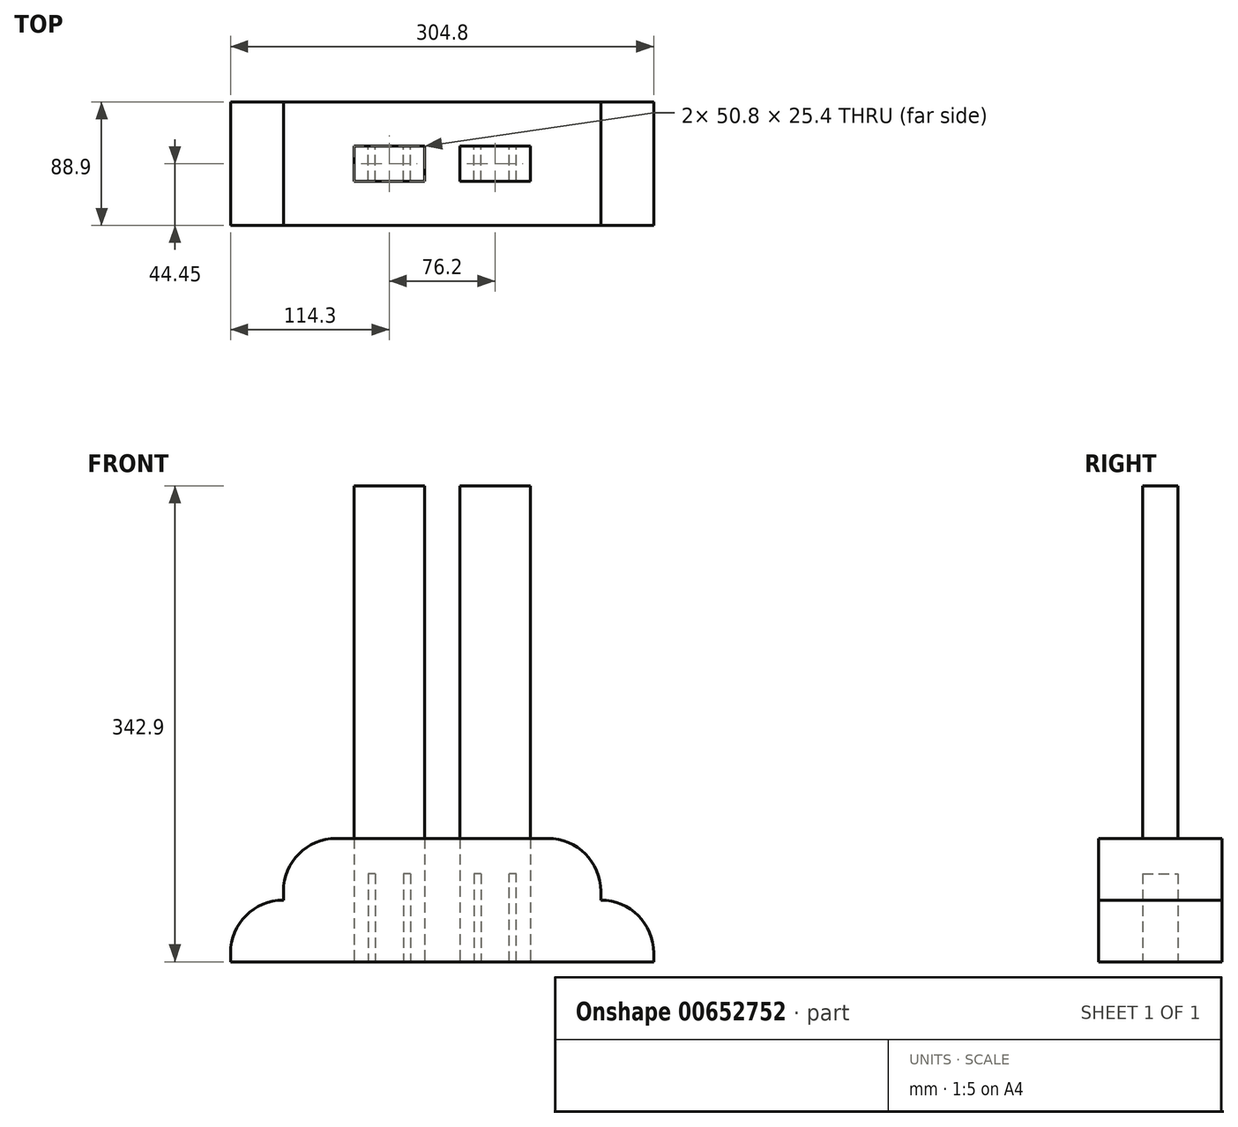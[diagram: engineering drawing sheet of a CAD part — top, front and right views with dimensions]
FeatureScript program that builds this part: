
annotation { "Feature Type Name" : "Feature", "Feature Type Description" : "" }
export const myFeature = defineFeature(function(context is Context, id is Id, definition is map)
    precondition{}
    {
        {
            var Q0;
            Q0=qCreatedBy(makeId("Front.planeOp"),FACE);
            var sketch = newSketch(context, id + "F0", { "sketchPlane" : qUnion([Q0])});
            skLineSegment(sketch, "E0.bottom", {"start": v(152.4, -44.45) * mm, "end": v(-152.4, -44.45) * mm});
            skLineSegment(sketch, "E0.top", {"start": v(76.2, 44.45) * mm, "end": v(-76.2, 44.45) * mm});
            skLineSegment(sketch, "E0.left", {"start": v(152.4, -44.45) * mm, "end": v(152.4, -38.1) * mm});
            skLineSegment(sketch, "E0.right", {"start": v(-152.4, -44.45) * mm, "end": v(-152.4, -38.1) * mm});
            skPoint(sketch, "E0.middle", {"position": v(0, 0) * mm});
            skLineSegment(sketch, "E1", {"start": v(114.3, 0) * mm, "end": v(114.3, 0) * mm});
            skLineSegment(sketch, "E2", {"start": v(-114.3, 6.35) * mm, "end": v(-114.3, 0) * mm});
            skPoint(sketch, "E3.newPointA", {"position": v(-152.4, 44.45) * mm});
            skArc(sketch, "E3.filletArc", {"start": v(-76.2, 44.45) * mm, "mid": v(-103.14, 33.3) * mm, "end": v(-114.3, 6.35) * mm});
            skPoint(sketch, "E4.orphan", {"position": v(-152.4, 0) * mm});
            skArc(sketch, "E5.filletArc", {"start": v(-114.3, 0) * mm, "mid": v(-141.24, -11.16) * mm, "end": v(-152.4, -38.1) * mm});
            skArc(sketch, "E6.MirrorCS", {"start": v(114.3, 0) * mm, "mid": v(141.24, -11.16) * mm, "end": v(152.4, -38.1) * mm});
            skArc(sketch, "E7.MirrorCS", {"start": v(76.2, 44.45) * mm, "mid": v(103.14, 33.3) * mm, "end": v(114.3, 6.35) * mm});
            skLineSegment(sketch, "E8.MirrorCS", {"start": v(114.3, 6.35) * mm, "end": v(114.3, 0) * mm});
            skPoint(sketch, "E9.orphan", {"position": v(152.4, 44.45) * mm});
            skPoint(sketch, "E10.orphan", {"position": v(152.4, 0) * mm});
            skSolve(sketch);
        }
        {
            var Q0;
            Q0=makeQuery(id+"F0.imprint","IMPRINT",FACE,{"disambiguationData":[TD([[makeQuery(id+"F0.imprint","IMPRINT",EDGE,{"derivedFrom":sQuery(id+"F0.wireOp",EDGE,"E0.bottom")}),-1.0]])]});
            extrude(context, id + "F1", {"entities" : qUnion([Q0]), "depth" : 88.9 * mm, "offsetDistance" : 25.4 * mm});
        }
        {
            var Q0;
            Q0=makeQuery(id+"F1.opExtrude","SWEPT_FACE",FACE,{"disambiguationData":[OSD([sQuery(id+"F0.wireOp",EDGE,"E0.top")])]});
            var sketch = newSketch(context, id + "F2", { "sketchPlane" : qUnion([Q0])});
            skLineSegment(sketch, "E11.0", {"start": v(-63.5, -57.15) * mm, "end": v(-63.5, -31.75) * mm});
            skLineSegment(sketch, "E12.0", {"start": v(-12.7, -57.15) * mm, "end": v(-12.7, -31.75) * mm});
            skLineSegment(sketch, "E13.MirrorCS", {"start": v(12.7, -57.15) * mm, "end": v(12.7, -31.75) * mm});
            skLineSegment(sketch, "E14.MirrorCS", {"start": v(63.5, -57.15) * mm, "end": v(63.5, -31.75) * mm});
            skLineSegment(sketch, "E15.0", {"start": v(63.5, -31.75) * mm, "end": v(12.7, -31.75) * mm});
            skLineSegment(sketch, "E16.0", {"start": v(82.55, 6.35) * mm, "end": v(-82.55, 6.35) * mm});
            skLineSegment(sketch, "E16.1", {"start": v(82.55, -95.25) * mm, "end": v(82.55, 6.35) * mm});
            skLineSegment(sketch, "E16.2", {"start": v(-82.55, -95.25) * mm, "end": v(82.55, -95.25) * mm});
            skLineSegment(sketch, "E16.3", {"start": v(-82.55, 6.35) * mm, "end": v(-82.55, -95.25) * mm});
            skLineSegment(sketch, "E17.0", {"start": v(63.5, -57.15) * mm, "end": v(12.7, -57.15) * mm});
            skPoint(sketch, "E18.orphan", {"position": v(-63.5, 0) * mm});
            skPoint(sketch, "E19.orphan", {"position": v(-63.5, -88.9) * mm});
            skPoint(sketch, "E20.orphan", {"position": v(-12.7, -88.9) * mm});
            skLineSegment(sketch, "E21.trimOffspring", {"start": v(-12.7, -57.15) * mm, "end": v(-63.5, -57.15) * mm});
            skLineSegment(sketch, "E22.trimOffspring", {"start": v(-12.7, -31.75) * mm, "end": v(-63.5, -31.75) * mm});
            skPoint(sketch, "E23.orphan", {"position": v(-12.7, 0) * mm});
            skPoint(sketch, "E24.orphan", {"position": v(12.7, 0) * mm});
            skPoint(sketch, "E25.orphan", {"position": v(63.5, 0) * mm});
            skPoint(sketch, "E26.orphan", {"position": v(63.5, -88.9) * mm});
            skPoint(sketch, "E27.orphan", {"position": v(12.7, -88.9) * mm});
            skSolve(sketch);
        }
        {
            var Q0;
            Q0=makeQuery(id+"F2.imprint","IMPRINT",FACE,{"disambiguationData":[TD([[makeQuery(id+"F2.imprint","IMPRINT",EDGE,{"derivedFrom":sQuery(id+"F2.wireOp",EDGE,"E11.0")}),-1.0]])]});
            var Q1;
            Q1=makeQuery(id+"F2.imprint","IMPRINT",FACE,{"disambiguationData":[TD([[makeQuery(id+"F2.imprint","IMPRINT",EDGE,{"derivedFrom":sQuery(id+"F2.wireOp",EDGE,"E13.MirrorCS")}),-1.0]])]});
            extrude(context, id + "F3", {"entities" : qUnion([Q0, Q1]), "operationType" : NewBodyOperationType.REMOVE, "endBound" : BoundingType.THROUGH_ALL, "oppositeDirection" : true, "depth" : 25.4 * mm, "offsetDistance" : 25.4 * mm});
        }
        {
            var Q0;
            Q0=makeQuery(id+"F2.imprint","IMPRINT",FACE,{"disambiguationData":[TD([[makeQuery(id+"F2.imprint","IMPRINT",EDGE,{"derivedFrom":sQuery(id+"F2.wireOp",EDGE,"E11.0")}),-1.0]])]});
            var Q1;
            Q1=makeQuery(id+"F2.imprint","IMPRINT",FACE,{"disambiguationData":[TD([[makeQuery(id+"F2.imprint","IMPRINT",EDGE,{"derivedFrom":sQuery(id+"F2.wireOp",EDGE,"E13.MirrorCS")}),-1.0]])]});
            extrude(context, id + "F4", {"entities" : qUnion([Q0, Q1]), "depth" : 254 * mm, "offsetDistance" : 25.4 * mm, "hasSecondDirection" : true, "secondDirectionOppositeDirection" : true, "secondDirectionDepth" : 88.9 * mm});
        }
        {
            var Q0;
            Q0=makeQuery(id+"F4.opExtrude","CAP_FACE",FACE,{"disambiguationData":[OSD([sQuery(id+"F2.wireOp",EDGE,"E11.0"),sQuery(id+"F2.wireOp",EDGE,"E12.0"),sQuery(id+"F2.wireOp",EDGE,"E21.trimOffspring"),sQuery(id+"F2.wireOp",EDGE,"E22.trimOffspring")])],"isStart":true});
            var sketch = newSketch(context, id + "F5", { "sketchPlane" : qUnion([Q0])});
            skLineSegment(sketch, "E28.0", {"start": v(-53.34, 57.15) * mm, "end": v(-53.34, 31.75) * mm});
            skLineSegment(sketch, "E29.0", {"start": v(-48.26, 57.15) * mm, "end": v(-48.26, 31.75) * mm});
            skLineSegment(sketch, "E30.0", {"start": v(-38.1, 57.15) * mm, "end": v(-38.1, 31.75) * mm});
            skLineSegment(sketch, "E31.MirrorCS", {"start": v(-27.94, 57.15) * mm, "end": v(-27.94, 31.75) * mm});
            skLineSegment(sketch, "E32.MirrorCS", {"start": v(-22.86, 57.15) * mm, "end": v(-22.86, 31.75) * mm});
            skLineSegment(sketch, "E33.MirrorCS", {"start": v(22.86, 57.15) * mm, "end": v(22.86, 31.75) * mm});
            skLineSegment(sketch, "E34.MirrorCS", {"start": v(27.94, 57.15) * mm, "end": v(27.94, 31.75) * mm});
            skLineSegment(sketch, "E35.MirrorCS", {"start": v(38.1, 57.15) * mm, "end": v(38.1, 31.75) * mm});
            skLineSegment(sketch, "E36.MirrorCS", {"start": v(48.26, 57.15) * mm, "end": v(48.26, 31.75) * mm});
            skLineSegment(sketch, "E37.MirrorCS", {"start": v(53.34, 57.15) * mm, "end": v(53.34, 31.75) * mm});
            skSolve(sketch);
        }
        {
            var Q0;
            {var subQ0=sQuery(id+"F5.wireOp",EDGE,"E28.0");Q0=makeQuery(id+"F5.imprint","IMPRINT",FACE,{"disambiguationData":[TD([[makeQuery(id+"F5.imprint","IMPRINT",EDGE,{"derivedFrom":subQ0}),1.0]])]});}
            var Q1;
            {var subQ0=sQuery(id+"F5.wireOp",EDGE,"E31.MirrorCS");Q1=makeQuery(id+"F5.imprint","IMPRINT",FACE,{"disambiguationData":[TD([[makeQuery(id+"F5.imprint","IMPRINT",EDGE,{"derivedFrom":subQ0}),1.0]])]});}
            extrude(context, id + "F6", {"entities" : qUnion([Q0, Q1]), "operationType" : NewBodyOperationType.REMOVE, "oppositeDirection" : true, "depth" : 63.5 * mm, "offsetDistance" : 25.4 * mm});
        }
        {
            var Q0;
            Q0=makeQuery(id+"F4.opExtrude","CAP_FACE",FACE,{"disambiguationData":[OSD([sQuery(id+"F2.wireOp",EDGE,"E13.MirrorCS"),sQuery(id+"F2.wireOp",EDGE,"E14.MirrorCS"),sQuery(id+"F2.wireOp",EDGE,"E15.0"),sQuery(id+"F2.wireOp",EDGE,"E17.0")])],"isStart":true});
            var sketch = newSketch(context, id + "F7", { "sketchPlane" : qUnion([Q0])});
            skLineSegment(sketch, "E38.0", {"start": v(22.86, 57.15) * mm, "end": v(22.86, 31.75) * mm});
            skLineSegment(sketch, "E39.0", {"start": v(27.94, 57.15) * mm, "end": v(27.94, 31.75) * mm});
            skLineSegment(sketch, "E40.0", {"start": v(38.1, 57.15) * mm, "end": v(38.1, 31.75) * mm});
            skLineSegment(sketch, "E41.MirrorCS", {"start": v(48.26, 57.15) * mm, "end": v(48.26, 31.75) * mm});
            skLineSegment(sketch, "E42.MirrorCS", {"start": v(53.34, 57.15) * mm, "end": v(53.34, 31.75) * mm});
            skSolve(sketch);
        }
        {
            var Q0;
            {var subQ0=sQuery(id+"F7.wireOp",EDGE,"E38.0");Q0=makeQuery(id+"F7.imprint","IMPRINT",FACE,{"disambiguationData":[TD([[makeQuery(id+"F7.imprint","IMPRINT",EDGE,{"derivedFrom":subQ0}),1.0]])]});}
            var Q1;
            {var subQ0=sQuery(id+"F7.wireOp",EDGE,"E41.MirrorCS");Q1=makeQuery(id+"F7.imprint","IMPRINT",FACE,{"disambiguationData":[TD([[makeQuery(id+"F7.imprint","IMPRINT",EDGE,{"derivedFrom":subQ0}),1.0]])]});}
            extrude(context, id + "F8", {"entities" : qUnion([Q0, Q1]), "operationType" : NewBodyOperationType.REMOVE, "oppositeDirection" : true, "depth" : 63.5 * mm, "offsetDistance" : 25.4 * mm});
        }
        {
            var Q0;
            Q0=makeQuery(id+"F6.boolean.opBoolean","COPY",FACE,{"derivedFrom":makeQuery(id+"F6.opExtrude","CAP_FACE",FACE,{"disambiguationData":[OSD([sQuery(id+"F2.wireOp",EDGE,"E21.trimOffspring"),sQuery(id+"F2.wireOp",EDGE,"E22.trimOffspring"),sQuery(id+"F5.wireOp",EDGE,"E28.0"),sQuery(id+"F5.wireOp",EDGE,"E29.0")])],"isStart":false})});
            var sketch = newSketch(context, id + "F9", { "sketchPlane" : qUnion([Q0])});
            skSolve(sketch);
        }
        {
            var Q0;
            Q0=makeQuery(id+"F6.boolean.opBoolean","COPY",FACE,{"derivedFrom":makeQuery(id+"F6.opExtrude","CAP_FACE",FACE,{"disambiguationData":[OSD([sQuery(id+"F2.wireOp",EDGE,"E21.trimOffspring"),sQuery(id+"F2.wireOp",EDGE,"E22.trimOffspring"),sQuery(id+"F5.wireOp",EDGE,"E31.MirrorCS"),sQuery(id+"F5.wireOp",EDGE,"E32.MirrorCS")])],"isStart":false})});
            var Q1;
            {var subQ0=sQuery(id+"F5.wireOp",EDGE,"E28.0");Q1=makeQuery(id+"F9.imprint","IMPRINT",FACE,{"disambiguationData":[TD([[makeQuery(id+"F9.imprint","IMPRINT",EDGE,{"derivedFrom":makeQuery(id+"F6.boolean.opBoolean","COPY",EDGE,{"derivedFrom":makeQuery(id+"F6.opExtrude","CAP_EDGE",EDGE,{"disambiguationData":[OSD([subQ0])],"isStart":false})})}),1.0]])]});}
            var Q2;
            Q2=makeQuery(id+"F8.boolean.opBoolean","COPY",FACE,{"derivedFrom":makeQuery(id+"F8.opExtrude","CAP_FACE",FACE,{"disambiguationData":[OSD([sQuery(id+"F2.wireOp",EDGE,"E15.0"),sQuery(id+"F2.wireOp",EDGE,"E17.0"),sQuery(id+"F7.wireOp",EDGE,"E38.0"),sQuery(id+"F7.wireOp",EDGE,"E39.0")])],"isStart":false})});
            var Q3;
            Q3=makeQuery(id+"F8.boolean.opBoolean","COPY",FACE,{"derivedFrom":makeQuery(id+"F8.opExtrude","CAP_FACE",FACE,{"disambiguationData":[OSD([sQuery(id+"F2.wireOp",EDGE,"E15.0"),sQuery(id+"F2.wireOp",EDGE,"E17.0"),sQuery(id+"F7.wireOp",EDGE,"E41.MirrorCS"),sQuery(id+"F7.wireOp",EDGE,"E42.MirrorCS")])],"isStart":false})});
            extrude(context, id + "F10", {"entities" : qUnion([Q0, Q1, Q2, Q3]), "depth" : 63.5 * mm, "offsetDistance" : 25.4 * mm});
        }
    });
